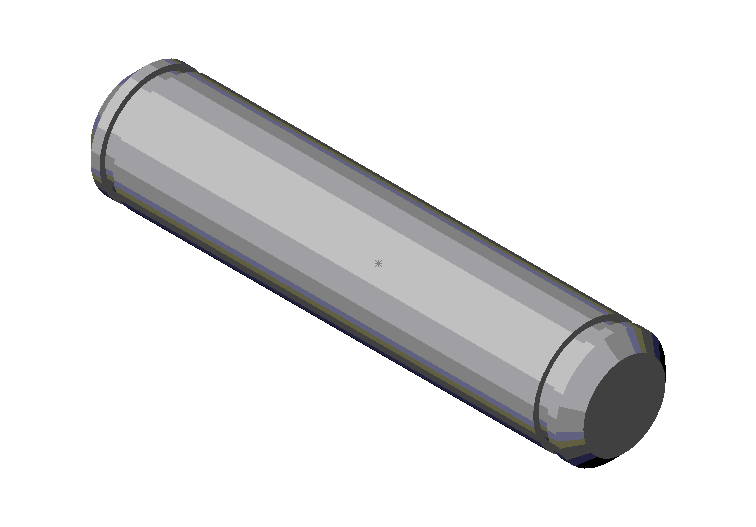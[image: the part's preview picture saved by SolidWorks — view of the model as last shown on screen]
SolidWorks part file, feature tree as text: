
SOLIDWORKS PART (.sldprt)
format: sldprt  version: not decoded by parser v0  size: 93,696 bytes
history: native  units: mm
features: plane x5, sketch x3, cut_extrude x2, material x1, extrude x1, chamfer x1 (+8 scaffold rows collapsed)
feature tree (21):
  scaffold x8  (default folders/planes/origin — collapsed)
  material  "Matériau <non spécifié>"
  plane  "Face"
  plane  "Dessus"
  plane  "Droite"
  sketch  "Esquisse2"  dims[D1=6.0mm]
  extrude  "Base-Extrusion"  Depth=27mm
  plane  "Plan4"  Offset=12.25mm
  sketch  "Esquisse3"  dims[D1=5.4mm]
  cut_extrude  "Enlèv. mat.-Extru.1"  Depth=0.75mm
  plane  "Plan5"  Offset=24.5mm
  sketch  "Esquisse4"  dims[D1=5.4mm]
  cut_extrude  "Enlèv. mat.-Extru.2"  Depth=0.75mm
  chamfer  "Chanfrein3"  Distance=0.75mm Angle=45deg
decode coverage: 7 of 7 modeling features carry decoded parameters
note: suppression state not decoded; provenance and decode notes live in map.json
